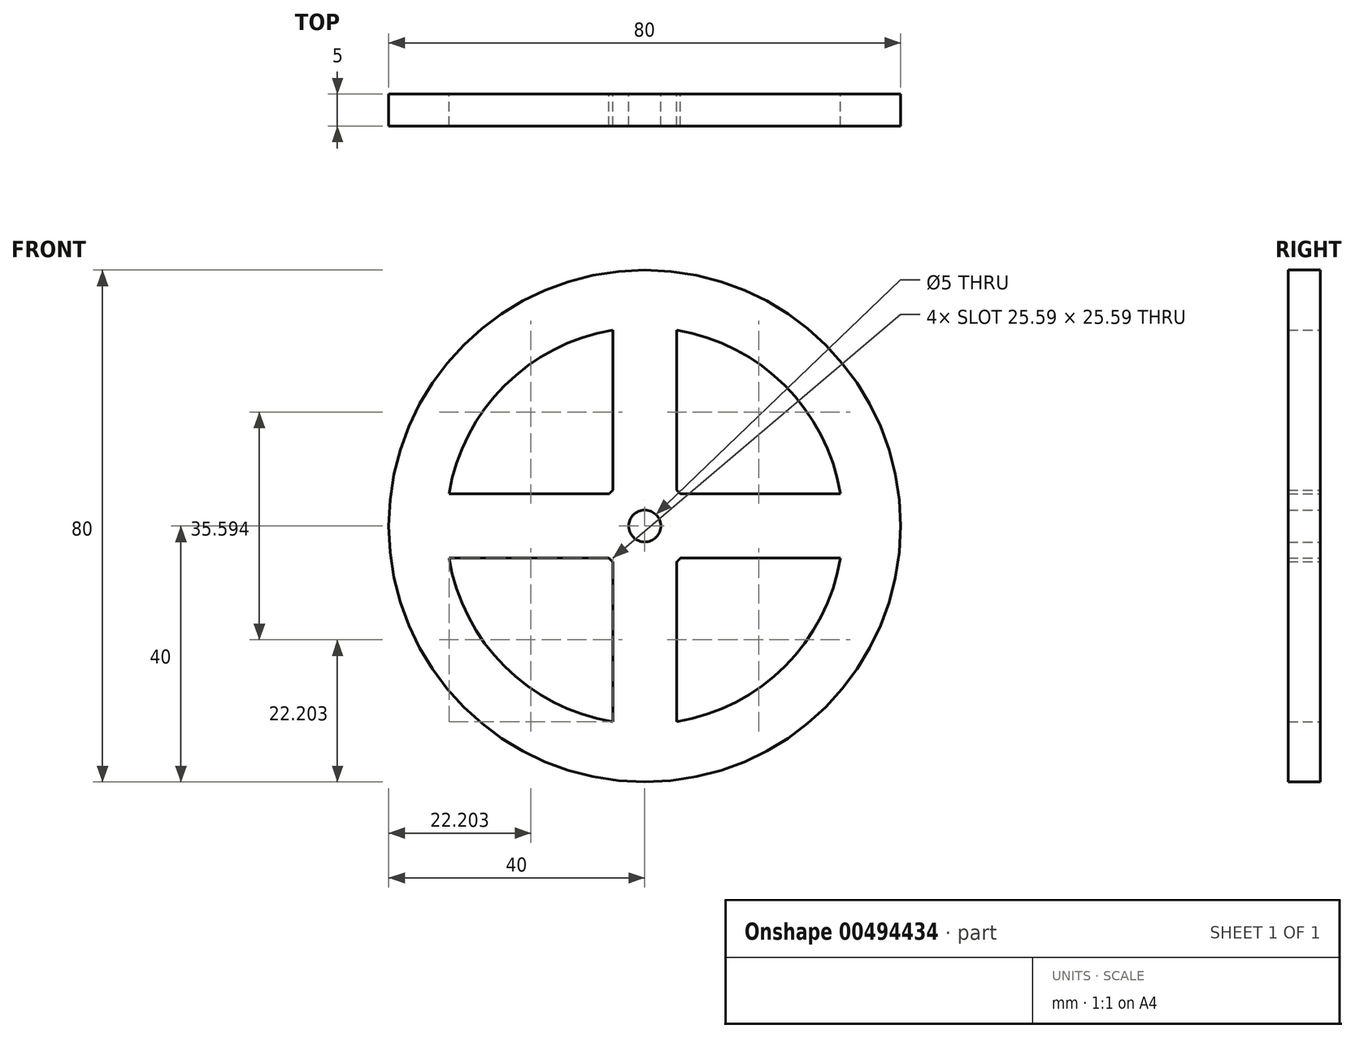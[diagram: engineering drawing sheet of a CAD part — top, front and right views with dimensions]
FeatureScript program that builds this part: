
annotation { "Feature Type Name" : "Feature", "Feature Type Description" : "" }
export const myFeature = defineFeature(function(context is Context, id is Id, definition is map)
    precondition{}
    {
        {
            var Q0;
            Q0=qCreatedBy(makeId("Front.planeOp"),FACE);
            var sketch = newSketch(context, id + "F0", { "sketchPlane" : qUnion([Q0])});
            skCircle(sketch, "E0", {"center": v(0, 0) * mm, "radius": 40 * mm});
            skArc(sketch, "E1", {"start": v(-5, 30.6) * mm, "mid": v(-21.92, 21.92) * mm, "end": v(-30.6, 5) * mm});
            skArc(sketch, "E2", {"start": v(5, -5.6) * mm, "mid": v(5.3, -5.3) * mm, "end": v(5.6, -5) * mm});
            skCircle(sketch, "E3", {"center": v(0, 0) * mm, "radius": 2.5 * mm});
            skLineSegment(sketch, "E4", {"start": v(0, 0) * mm, "end": v(0, 31) * mm});
            skLineSegment(sketch, "E5", {"start": v(0, 31) * mm, "end": v(0, 0) * mm});
            skLineSegment(sketch, "E6", {"start": v(0, 0) * mm, "end": v(31, 0) * mm});
            skLineSegment(sketch, "E7", {"start": v(0, 0) * mm, "end": v(0, -31) * mm});
            skLineSegment(sketch, "E8", {"start": v(0, 0) * mm, "end": v(-31, 0) * mm});
            skLineSegment(sketch, "E9.0", {"start": v(5, 30.6) * mm, "end": v(5, 5.6) * mm});
            skLineSegment(sketch, "E10.0", {"start": v(-5.6, 5) * mm, "end": v(-30.6, 5) * mm});
            skLineSegment(sketch, "E11.0", {"start": v(-5, 30.6) * mm, "end": v(-5, 5.6) * mm});
            skLineSegment(sketch, "E12.0", {"start": v(5.6, -5) * mm, "end": v(30.6, -5) * mm});
            skLineSegment(sketch, "E13.0", {"start": v(5.6, 5) * mm, "end": v(30.6, 5) * mm});
            skLineSegment(sketch, "E14.0", {"start": v(-5, -5.6) * mm, "end": v(-5, -30.6) * mm});
            skLineSegment(sketch, "E15.0", {"start": v(-5.6, -5) * mm, "end": v(-30.6, -5) * mm});
            skArc(sketch, "E16.trimOffspring", {"start": v(-30.6, -5) * mm, "mid": v(-21.92, -21.92) * mm, "end": v(-5, -30.6) * mm});
            skArc(sketch, "E17.trimOffspring", {"start": v(5, -30.6) * mm, "mid": v(21.92, -21.92) * mm, "end": v(30.6, -5) * mm});
            skArc(sketch, "E18.trimOffspring", {"start": v(30.6, 5) * mm, "mid": v(21.92, 21.92) * mm, "end": v(5, 30.6) * mm});
            skArc(sketch, "E19.trimOffspring", {"start": v(5.6, 5) * mm, "mid": v(5.3, 5.3) * mm, "end": v(5, 5.6) * mm});
            skArc(sketch, "E20.trimOffspring", {"start": v(-5, 5.6) * mm, "mid": v(-5.3, 5.3) * mm, "end": v(-5.6, 5) * mm});
            skArc(sketch, "E21.trimOffspring", {"start": v(-5.6, -5) * mm, "mid": v(-5.3, -5.3) * mm, "end": v(-5, -5.6) * mm});
            skLineSegment(sketch, "E22.trimOffspring", {"start": v(5, -5.6) * mm, "end": v(5, -30.6) * mm});
            skSolve(sketch);
        }
        {
            var Q0;
            Q0=makeQuery(id+"F0.imprint","IMPRINT",FACE,{"disambiguationData":[TD([[makeQuery(id+"F0.imprint","IMPRINT",EDGE,{"derivedFrom":sQuery(id+"F0.wireOp",EDGE,"E0")}),1.0]])]});
            extrude(context, id + "F1", {"entities" : qUnion([Q0]), "endBound" : BoundingType.SYMMETRIC, "depth" : 5 * mm});
        }
    });
